# Revit family: HL_Корпус плоского душевого лотка InFloor_HL53KV
name_source: partatom
category: Instalační zařizovací předměty
revit_build: Autodesk Revit 2016 (Build: 20151007_0715(x64)
units: mm (PartAtom-declared; Revit-internal decimal feet)

## family parameters
Bod výpočtu místnosti = Ano
Kóta kulaté spojky = Použít průměr
Nadpis OmniClass = General Pipework and Ductwork Products
Ořezat dutým tvarem při načtení = Ne
Sdílené = Ne
Typ součásti = Normální
Vždy vertikální = Ano
Založené na pracovní rovině = Ne
Číslo OmniClass = 23.60.30.00

## types (2) — shared parameters
F = HL_Решётка душевого лотка InFloor Стандарт_HL053S : HL_Решётка душевого лотка InFloor Стандарт_HL053S_90
G = HL_Решётка душевого лотка InFloor Стандарт_HL053S : HL_Решётка душевого лотка InFloor Стандарт_HL053S_100
H = HL_Решётка душевого лотка InFloor Стандарт_HL053S : HL_Решётка душевого лотка InFloor Стандарт_HL053S_120
HL052_тип = HL_Pешётка InFloor_HL052 : HL_Решётка душевого лотка InFloor матовая_HL052M
I = HL_Решётка душевого лотка InFloor стандарт_HL053WS : HL_Решётка душевого лотка InFloor стандарт_HL053WS_90
J = HL_Решётка душевого лотка InFloor стандарт_HL053WS : HL_Решётка душевого лотка InFloor стандарт_HL053WS_100
K = HL_Решётка душевого лотка InFloor стандарт_HL053WS : HL_Решётка душевого лотка InFloor стандарт_HL053WS_120
Popis = Корпус плоского душевого лотка InFloor CeraDrain, DN40
URL = http://www.hutterer-lechner.com
Výrobce = HL Hutterer & Lechner GmbH
МАТЕРИАЛ = PP
НОМИНАЛЬНЫЙ ДИАМЕТР = 50 mm
ПРОПУСКНАЯ СПОСОБНОСТЬ = 0.0 m³/h
РАЗМЕР = DN50
zero-valued in all types: Cena

## per-type parameters (varying)
| type | BO | EAN | HL053_тип | Klíčová poznámka | Komentáře k typům | Model | ВЕС | ВЫСОТА МОНТАЖА | ПРОИЗВОДИТЕЛЬНОСТЬ |
| HL_Корпус плоского душевого лотка InFloor_HL53KV | HL_53KV | 9003076047154 | HL_Решётка душевого лотка InFloor матовая_HL053M : HL_Решётка душевого лотка InFloor матовая_HL053M_120 | HL53KV | Корпус душевого лотка InFloor, DN50, verticale | HL53KV | 1,5 kg | 30-143mm | 0,98l/s |
| HL_Корпус плоского душевого лотка InFloor_HL53KVC | HL_53KV : HL_53KVC | 9003076047833 | HL_Решётка душевого лотка InFloor матовая_HL053M : HL_Решётка душевого лотка InFloor матовая_HL053M_85 | HL53KVC | Корпус душевого лотка InFloor CeraDrain, DN50 | HL53KVC | 4,3 kg | 30-131mm | 1 l/s |
